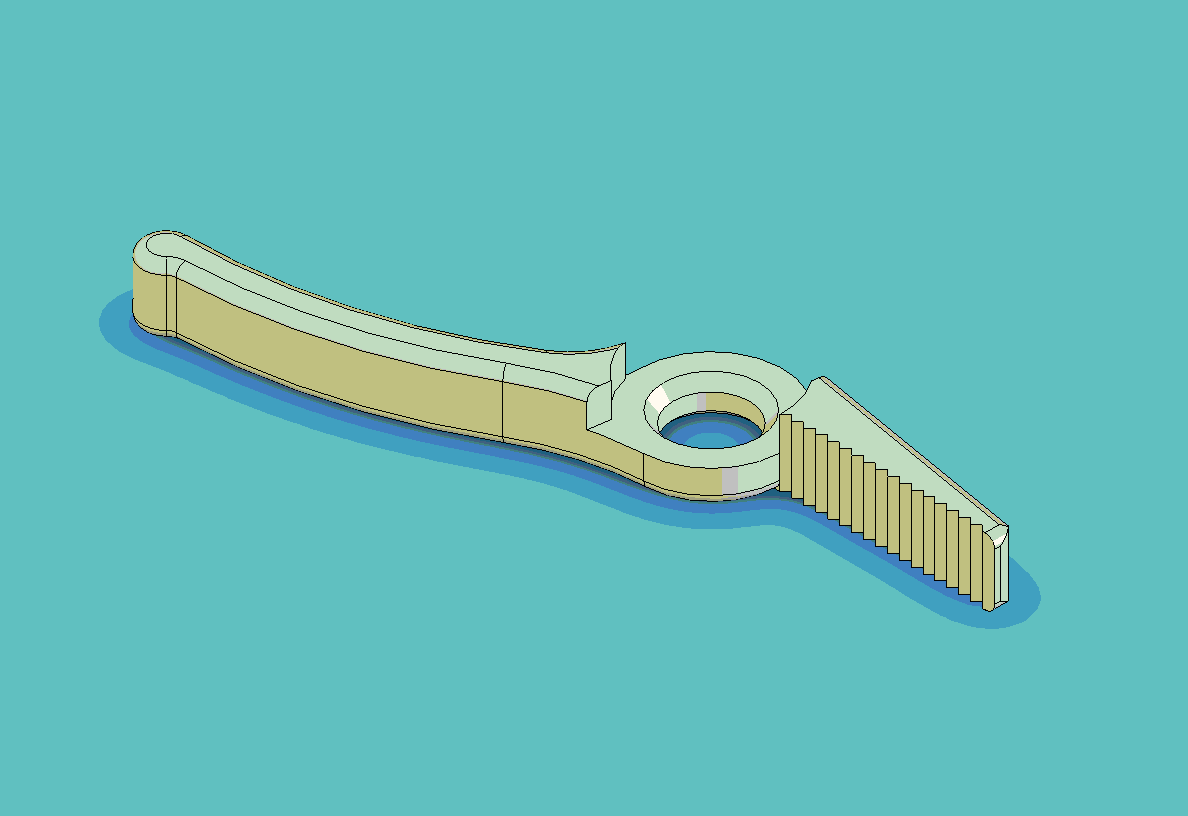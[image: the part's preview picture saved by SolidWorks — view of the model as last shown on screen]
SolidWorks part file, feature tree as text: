
SOLIDWORKS PART (.sldprt)
format: sldprt  version: not decoded by parser v0  size: 388,608 bytes
history: native  units: mm
features: sketch x5, fillet x4, cut_extrude x4, chamfer x2, material x1, extrude x1 (+15 scaffold rows collapsed)
feature tree (32):
  scaffold x15  (default folders/planes/origin — collapsed)
  material  "ABS"
  sketch  "Sketch1"  dims[c1.D1=10.16mm c1.D2=19.05mm c1.D6=6.35mm c1.D8=~69.302049mm c2.D6=5.08mm c2.D3=38.1mm c2.D4=2.54mm c2.D5=~21.677049mm c2.D7=50.8mm c2.D9=50.8mm c2.D10=50.8mm c2.D8=5.08mm c2.D11=25.4mm c2.D12=25.4mm c3.D5=~14.852429mm c4.D5=60.0deg c4.D7=~0.396875mm c4.D8=28.575mm c4.D6=2.54mm c5.D7=2.54mm]
  extrude  "Extrude1"  Depth=8.89mm
  fillet  "Fillet3"  Radius=33.02mm
  sketch  "Sketch4"
  cut_extrude  "Cut-Extrude1"  Depth=4.4704mm
  fillet  "Fillet4"  Radius=1.27mm
  fillet  "Fillet7"  Radius=1.27mm
  fillet  "Fillet8"  Radius=2.54mm
  sketch  "Sketch6"  dims[D1=1.27mm]
  cut_extrude  "Cut-Extrude4"  [1 undecoded]
  sketch  "Sketch7"  dims[D1=19.1008mm]
  cut_extrude  "Cut-Extrude5"  [1 undecoded]
  chamfer  "Chamfer1"  Distance=0.762mm Angle=45deg
  chamfer  "Chamfer2"  Distance=1.27mm Angle=50deg
  sketch  "Sketch9"  dims[D1=1.5875mm]
  cut_extrude  "Cut-Extrude7"  [1 undecoded]
decode coverage: 12 of 16 modeling features carry decoded parameters
note: ~ marks probable driven/reference dimensions
note: 3 parameter values undecoded
summary: no parameter record found for 3 features
note: suppression state not decoded; provenance and decode notes live in map.json
